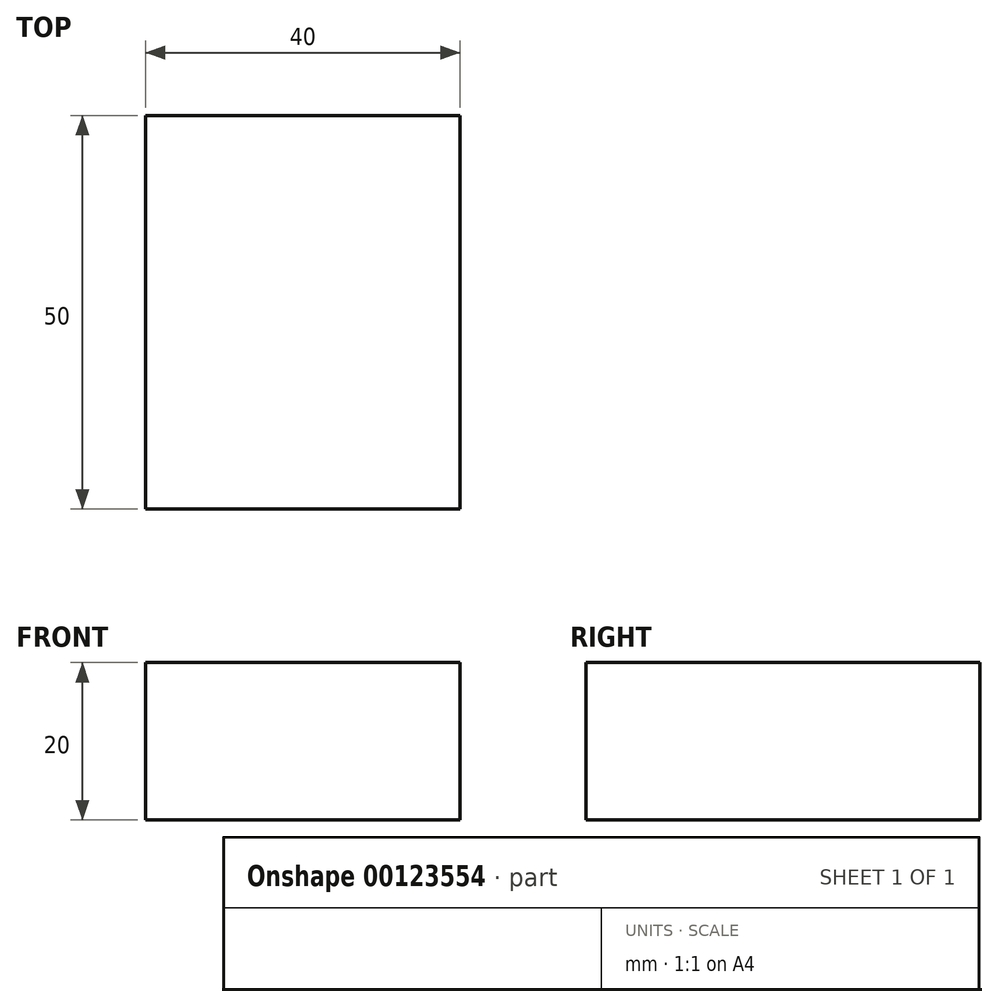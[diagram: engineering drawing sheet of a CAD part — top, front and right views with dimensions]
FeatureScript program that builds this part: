
annotation { "Feature Type Name" : "Feature", "Feature Type Description" : "" }
export const myFeature = defineFeature(function(context is Context, id is Id, definition is map)
    precondition{}
    {
        {
            var Q0;
            Q0=qCreatedBy(makeId("Top.planeOp"),FACE);
            var sketch = newSketch(context, id + "F0", { "sketchPlane" : qUnion([Q0])});
            skLineSegment(sketch, "E0.bottom", {"start": v(20, 25) * mm, "end": v(-20, 25) * mm});
            skLineSegment(sketch, "E0.top", {"start": v(20, -25) * mm, "end": v(-20, -25) * mm});
            skLineSegment(sketch, "E0.left", {"start": v(20, 25) * mm, "end": v(20, -25) * mm});
            skLineSegment(sketch, "E0.right", {"start": v(-20, 25) * mm, "end": v(-20, -25) * mm});
            skPoint(sketch, "E0.middle", {"position": v(0, 0) * mm});
            skSolve(sketch);
        }
        {
            var Q0;
            Q0 = qSketchRegion(id + "F0", true);
            extrude(context, id + "F1", {"entities" : qUnion([Q0]), "depth" : 20 * mm});
        }
    });
